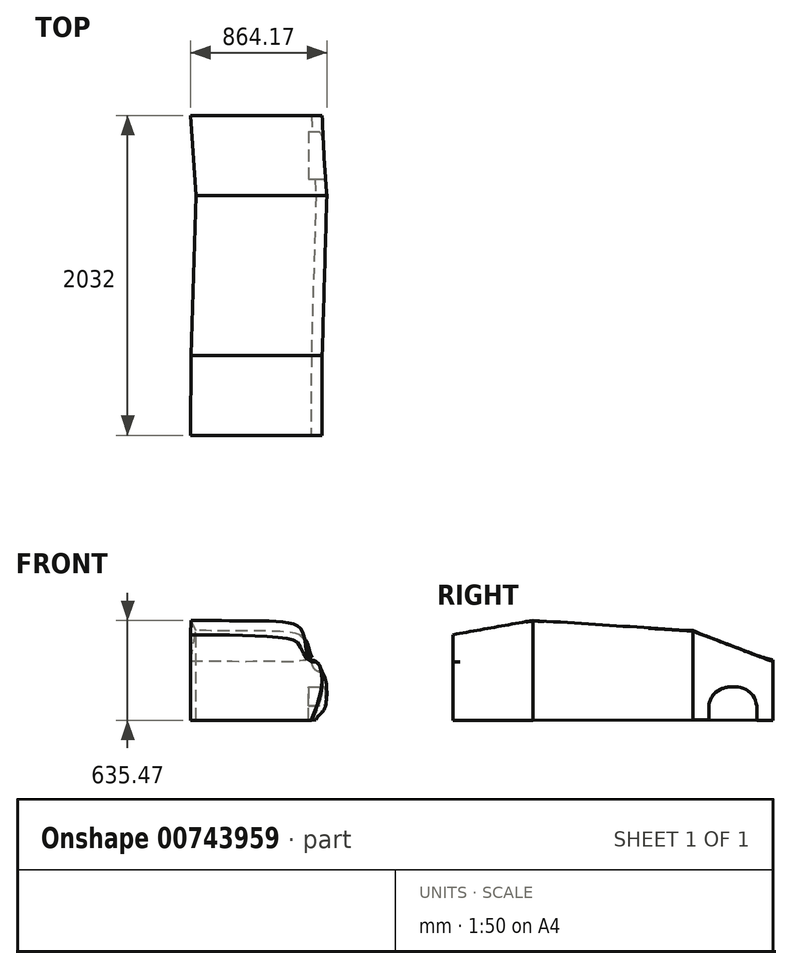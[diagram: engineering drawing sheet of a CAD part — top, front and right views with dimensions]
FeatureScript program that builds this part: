
annotation { "Feature Type Name" : "Feature", "Feature Type Description" : "" }
export const myFeature = defineFeature(function(context is Context, id is Id, definition is map)
    precondition{}
    {
        {
            var Q0;
            Q0=qCreatedBy(makeId("Front.planeOp"),FACE);
            var sketch = newSketch(context, id + "F0", { "sketchPlane" : qUnion([Q0])});
            skLineSegment(sketch, "E0", {"start": v(-281.87, -258.33) * mm, "end": v(479.46, -258.33) * mm});
            skLineSegment(sketch, "E1", {"start": v(-281.87, -258.33) * mm, "end": v(-281.87, 306.97) * mm});
            skFitSpline(sketch, "E2", {"points": [v(479.46, -258.33) * mm, v(526.4, -204.8) * mm, v(548.61, -60.45) * mm, v(518.47, 39.48) * mm, v(479.46, 55.34) * mm, v(445.5, 136.24) * mm, v(416.96, 247.28) * mm, v(321.78, 294.86) * mm, v(34.68, 304.38) * mm, v(-281.87, 306.97) * mm], "startDerivative": vector(511.68, 1120.68) * mm, "endDerivative": vector(-1857, -32.36) * mm});
            skSolve(sketch);
        }
        {
            var Q0;
            Q0=qCreatedBy(makeId("Front.planeOp"),FACE);
            cPlane(context, id + "F1", {"entities" : qUnion([Q0]), "cplaneType" : CPlaneType.OFFSET, "offset" : 1016 * mm, "width" : 152.4 * mm, "height" : 152.4 * mm});
        }
        {
            var Q0;
            Q0=qCreatedBy(makeId("Front.planeOp"),FACE);
            cPlane(context, id + "F2", {"entities" : qUnion([Q0]), "cplaneType" : CPlaneType.OFFSET, "offset" : 508 * mm, "oppositeDirection" : true, "width" : 152.4 * mm, "height" : 152.4 * mm});
        }
        {
            var Q0;
            Q0=qCreatedBy(id+"F1.planeOp",FACE);
            cPlane(context, id + "F3", {"entities" : qUnion([Q0]), "cplaneType" : CPlaneType.OFFSET, "offset" : 508 * mm, "width" : 152.4 * mm, "height" : 152.4 * mm});
        }
        {
            var Q0;
            Q0=qCreatedBy(id+"F1.planeOp",FACE);
            var sketch = newSketch(context, id + "F4", { "sketchPlane" : qUnion([Q0])});
            skLineSegment(sketch, "E3", {"start": v(-313.3, -262.69) * mm, "end": v(451.07, -262.69) * mm});
            skLineSegment(sketch, "E4", {"start": v(-313.3, -262.69) * mm, "end": v(-313.3, 372.31) * mm});
            skFitSpline(sketch, "E5", {"points": [v(451.07, -262.69) * mm, v(498.01, -139.45) * mm, v(520.22, 4.89) * mm, v(490.08, 104.82) * mm, v(451.07, 120.68) * mm, v(417.12, 201.58) * mm, v(388.57, 312.61) * mm, v(293.4, 360.2) * mm, v(6.3, 369.72) * mm, v(-313.3, 372.31) * mm], "startDerivative": vector(511.68, 1120.68) * mm, "endDerivative": vector(-1857, -32.36) * mm});
            skSolve(sketch);
        }
        {
            var Q0;
            Q0=qCreatedBy(id+"F3.planeOp",FACE);
            var sketch = newSketch(context, id + "F5", { "sketchPlane" : qUnion([Q0])});
            skLineSegment(sketch, "E6", {"start": v(-314.68, -262.69) * mm, "end": v(448.82, -262.69) * mm});
            skLineSegment(sketch, "E7", {"start": v(-314.68, -262.69) * mm, "end": v(-314.68, 280.58) * mm});
            skFitSpline(sketch, "E8", {"points": [v(448.82, -262.69) * mm, v(495.76, -139.45) * mm, v(517.97, 4.89) * mm, v(487.83, 104.82) * mm, v(448.82, 109.43) * mm, v(396.86, 170.06) * mm, v(360.71, 234.43) * mm, v(290.92, 260.32) * mm, v(34.27, 276.07) * mm, v(-314.68, 280.58) * mm], "startDerivative": vector(511.68, 1120.68) * mm, "endDerivative": vector(-1857, -32.36) * mm});
            skSolve(sketch);
        }
        {
            var Q0;
            Q0=qCreatedBy(id+"F2.planeOp",FACE);
            var sketch = newSketch(context, id + "F6", { "sketchPlane" : qUnion([Q0])});
            skLineSegment(sketch, "E9", {"start": v(-314.82, -262.69) * mm, "end": v(451.07, -262.69) * mm});
            skLineSegment(sketch, "E10", {"start": v(-314.82, -262.69) * mm, "end": v(-314.82, 110.44) * mm});
            skFitSpline(sketch, "E11", {"points": [v(451.07, -262.69) * mm, v(498.01, -139.45) * mm, v(520.22, 4.89) * mm, v(490.08, 104.82) * mm, v(451.07, 120.68) * mm, v(404.02, 118.47) * mm, v(341.1, 110.44) * mm, v(259.45, 110.44) * mm, v(-12.3, 110.44) * mm, v(-314.82, 110.44) * mm], "startDerivative": vector(511.68, 1120.68) * mm, "endDerivative": vector(-1857, -32.36) * mm});
            skSolve(sketch);
        }
        {
            var Q0;
            Q0=makeQuery(id+"F4.imprint","IMPRINT",FACE,{"disambiguationData":[TD([[makeQuery(id+"F4.imprint","IMPRINT",EDGE,{"derivedFrom":sQuery(id+"F4.wireOp",EDGE,"E3")}),1.0]])]});
            var Q1;
            Q1=makeQuery(id+"F5.imprint","IMPRINT",FACE,{"disambiguationData":[TD([[makeQuery(id+"F5.imprint","IMPRINT",EDGE,{"derivedFrom":sQuery(id+"F5.wireOp",EDGE,"E6")}),1.0]])]});
            loft(context, id + "F7", {"sheetProfilesArray" : [{ "sheetProfileEntities" : qUnion([Q0]) }, { "sheetProfileEntities" : qUnion([Q1]) }]});
        }
        {
            var Q1;
            Q1=makeQuery(id+"F0.imprint","IMPRINT",FACE,{"disambiguationData":[TD([[makeQuery(id+"F0.imprint","IMPRINT",EDGE,{"derivedFrom":sQuery(id+"F0.wireOp",EDGE,"E0")}),1.0]])]});
            var Q2;
            Q2=makeQuery(id+"F7.opLoft","CAP_FACE",FACE,{"disambiguationData":[OSD([makeQuery(id+"F4.imprint","IMPRINT",FACE,{"disambiguationData":[TD([[makeQuery(id+"F4.imprint","IMPRINT",EDGE,{"derivedFrom":sQuery(id+"F4.wireOp",EDGE,"E3")}),1.0]])]})])],"isStart":true});
            loft(context, id + "F8", {"operationType" : NewBodyOperationType.ADD, "sheetProfilesArray" : [{ "sheetProfileEntities" : qUnion([Q1]) }, { "sheetProfileEntities" : qUnion([Q2]) }]});
        }
        {
            var Q1;
            Q1=makeQuery(id+"F6.imprint","IMPRINT",FACE,{"disambiguationData":[TD([[makeQuery(id+"F6.imprint","IMPRINT",EDGE,{"derivedFrom":sQuery(id+"F6.wireOp",EDGE,"E9")}),1.0]])]});
            var Q2;
            Q2=makeQuery(id+"F8.opLoft","CAP_FACE",FACE,{"disambiguationData":[OSD([makeQuery(id+"F0.imprint","IMPRINT",FACE,{"disambiguationData":[TD([[makeQuery(id+"F0.imprint","IMPRINT",EDGE,{"derivedFrom":sQuery(id+"F0.wireOp",EDGE,"E0")}),1.0]])]})])],"isStart":true});
            loft(context, id + "F9", {"operationType" : NewBodyOperationType.ADD, "sheetProfilesArray" : [{ "sheetProfileEntities" : qUnion([Q1]) }, { "sheetProfileEntities" : qUnion([Q2]) }]});
        }
        {
            var Q0;
            Q0=qCreatedBy(makeId("Right.planeOp"),FACE);
            var sketch = newSketch(context, id + "F10", { "sketchPlane" : qUnion([Q0])});
            skLineSegment(sketch, "E12", {"start": v(108.2, -438.7) * mm, "end": v(108.2, -310.27) * mm});
            skLineSegment(sketch, "E13", {"start": v(108.2, -438.7) * mm, "end": v(411.86, -438.7) * mm});
            skLineSegment(sketch, "E14", {"start": v(411.86, -438.7) * mm, "end": v(411.86, -313.07) * mm});
            skFitSpline(sketch, "E15", {"points": [v(411.86, -313.07) * mm, v(283.4, -191.85) * mm, v(108.2, -310.27) * mm], "startDerivative": vector(-86.92, 498.14) * mm, "endDerivative": vector(-61.64, -561.92) * mm});
            skSolve(sketch);
        }
        {
            var Q0;
            Q0 = qSketchRegion(id + "F10", true);
            extrude(context, id + "F11", {"entities" : qUnion([Q0]), "depth" : 25.4 * mm, "offsetDistance" : 25.4 * mm});
        }
        {
            var Q0;
            Q0=makeQuery(id+"F11.opExtrude","SWEPT_BODY",BODY,{"disambiguationData":[OSD([sQuery(id+"F10.wireOp",EDGE,"E12"),sQuery(id+"F10.wireOp",EDGE,"E13"),sQuery(id+"F10.wireOp",EDGE,"E14"),sQuery(id+"F10.wireOp",EDGE,"E15")])]});
            transform(context, id + "F12", {"entities" : qUnion([Q0]), "transformType" : TransformType.TRANSLATION_3D, "dx" : 558.8 * mm, "dy" : -5.08 * mm, "dz" : 142.24 * mm, "makeCopy" : false});
        }
        {
            var Q0;
            Q0=makeQuery(id+"F11.opExtrude","CAP_FACE",FACE,{"disambiguationData":[OSD([sQuery(id+"F10.wireOp",EDGE,"E12"),sQuery(id+"F10.wireOp",EDGE,"E13"),sQuery(id+"F10.wireOp",EDGE,"E14"),sQuery(id+"F10.wireOp",EDGE,"E15")])],"isStart":false});
            extrude(context, id + "F13", {"entities" : qUnion([Q0]), "operationType" : NewBodyOperationType.REMOVE, "oppositeDirection" : true, "depth" : 152.4 * mm, "offsetDistance" : 25.4 * mm});
        }
    });
